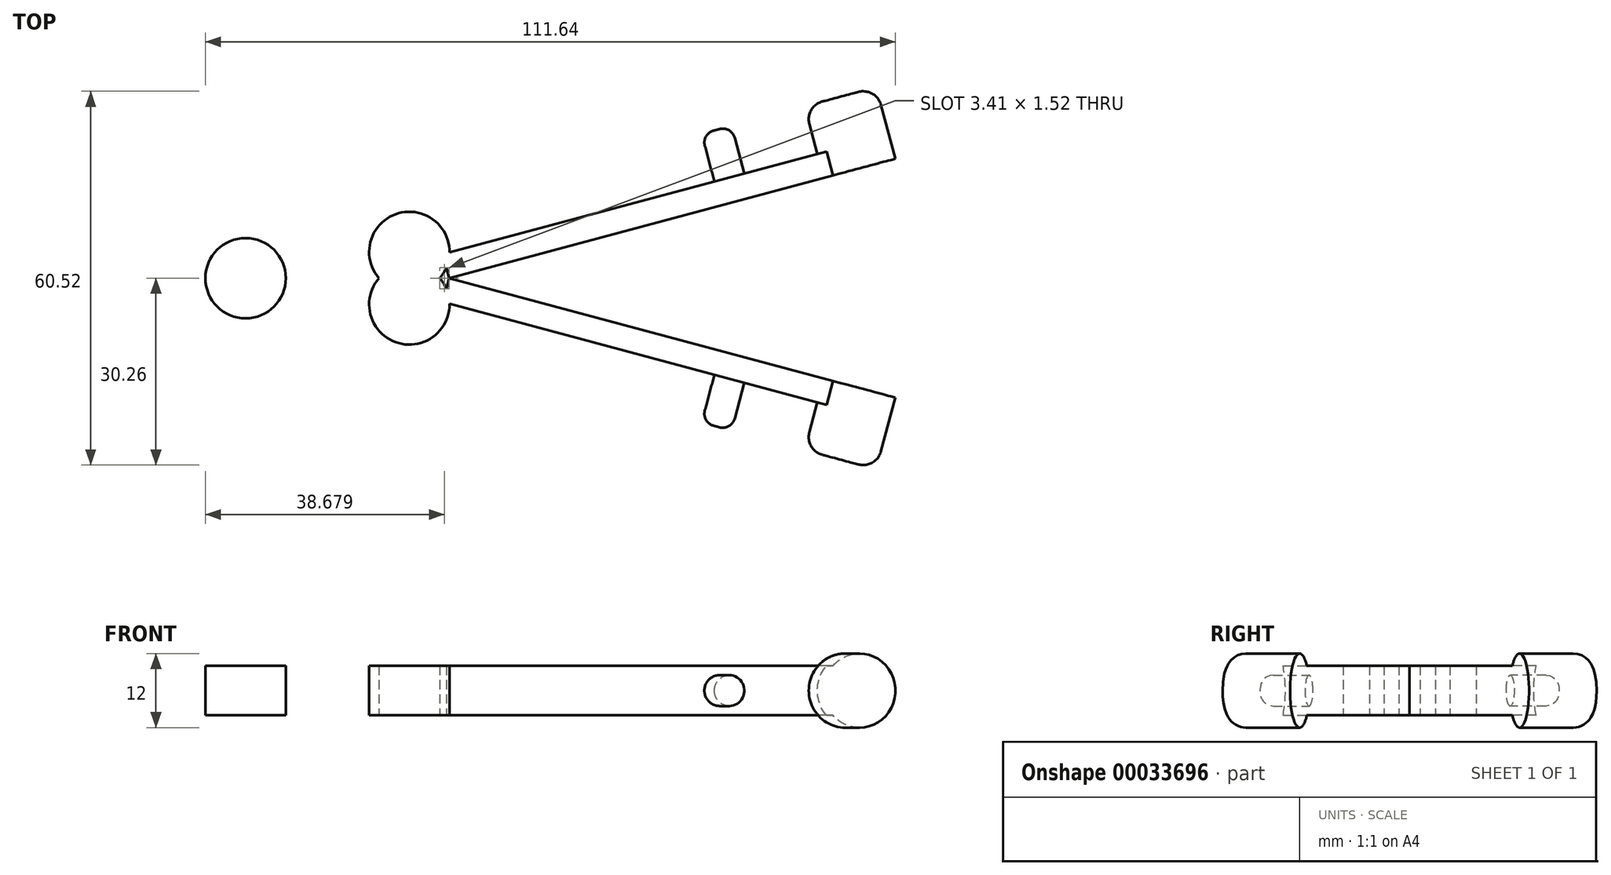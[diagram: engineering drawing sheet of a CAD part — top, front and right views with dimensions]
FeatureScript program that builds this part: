
annotation { "Feature Type Name" : "Feature", "Feature Type Description" : "" }
export const myFeature = defineFeature(function(context is Context, id is Id, definition is map)
    precondition{}
    {
        {
            var Q0;
            Q0=qCreatedBy(makeId("Top.planeOp"),FACE);
            var sketch = newSketch(context, id + "F0", { "sketchPlane" : qUnion([Q0])});
            skCircle(sketch, "E0", {"center": v(-26.5, 0) * mm, "radius": 6.5 * mm});
            skCircle(sketch, "E1", {"center": v(0, 4.25) * mm, "radius": 6.5 * mm});
            skCircle(sketch, "E2.MirrorC", {"center": v(0, -4.25) * mm, "radius": 6.5 * mm});
            skLineSegment(sketch, "E3", {"start": v(-26.3, 6.5) * mm, "end": v(-6.1, 6.5) * mm});
            skLineSegment(sketch, "E4.MirrorCS", {"start": v(-26.3, -6.5) * mm, "end": v(-6.1, -6.5) * mm});
            skLineSegment(sketch, "E5", {"start": v(6.36, 5.61) * mm, "end": v(6.5, -4.15) * mm});
            skLineSegment(sketch, "E6", {"start": v(6.44, 0) * mm, "end": v(47.77, 11.07) * mm});
            skSolve(sketch);
        }
        {
            var Q0;
            {var subQ0=sQuery(id+"F0.wireOp",EDGE,"E0");var subQ2=makeQuery(id+"F0.imprint","INTERSECT",VERTEX,{"derivedFrom":[subQ0,sQuery(id+"F0.wireOp",EDGE,"E3")]});Q0=makeQuery(id+"F0.imprint","IMPRINT",FACE,{"disambiguationData":[TD([[makeQuery(id+"F0.imprint","IMPRINT",EDGE,{"disambiguationData":[TD([[subQ2,-1.0]])],"derivedFrom":subQ0}),1.0]])]});}
            var Q1;
            {var subQ0=sQuery(id+"F0.wireOp",EDGE,"E2.MirrorC");var subQ1=sQuery(id+"F0.wireOp",EDGE,"E1");var subQ3=makeQuery(id+"F0.imprint","INTERSECT",VERTEX,{"disambiguationData":[OD(0.0)],"derivedFrom":[subQ1,subQ0]});Q1=makeQuery(id+"F0.imprint","IMPRINT",FACE,{"disambiguationData":[TD([[makeQuery(id+"F0.imprint","IMPRINT",EDGE,{"disambiguationData":[TD([[subQ3,-1.0]])],"derivedFrom":subQ1}),1.0]])]});}
            var Q2;
            {var subQ0=sQuery(id+"F0.wireOp",EDGE,"E5");var subQ1=sQuery(id+"F0.wireOp",EDGE,"E1");var subQ2=makeQuery(id+"F0.imprint","INTERSECT",VERTEX,{"disambiguationData":[OD(1.0)],"derivedFrom":[subQ1,subQ0]});Q2=makeQuery(id+"F0.imprint","IMPRINT",FACE,{"disambiguationData":[TD([[makeQuery(id+"F0.imprint","IMPRINT",EDGE,{"disambiguationData":[TD([[subQ2,1.0]])],"derivedFrom":subQ1}),-1.0]])]});}
            var Q3;
            {var subQ0=sQuery(id+"F0.wireOp",EDGE,"E3");Q3=makeQuery(id+"F0.imprint","IMPRINT",FACE,{"disambiguationData":[TD([[makeQuery(id+"F0.imprint","IMPRINT",EDGE,{"derivedFrom":subQ0}),-1.0]])]});}
            var Q4;
            {var subQ0=sQuery(id+"F0.wireOp",EDGE,"E2.MirrorC");var subQ3=sQuery(id+"F0.wireOp",EDGE,"E1");var subQ5=makeQuery(id+"F0.imprint","INTERSECT",VERTEX,{"disambiguationData":[OD(0.0)],"derivedFrom":[subQ3,subQ0]});Q4=makeQuery(id+"F0.imprint","IMPRINT",FACE,{"disambiguationData":[TD([[makeQuery(id+"F0.imprint","IMPRINT",EDGE,{"disambiguationData":[TD([[subQ5,-1.0]])],"derivedFrom":subQ3}),-1.0]])]});}
            var Q5;
            {var subQ1=sQuery(id+"F0.wireOp",EDGE,"E1");var subQ7=makeQuery(id+"F0.imprint","INTERSECT",VERTEX,{"derivedFrom":[subQ1,sQuery(id+"F0.wireOp",EDGE,"E3")]});Q5=makeQuery(id+"F0.imprint","IMPRINT",FACE,{"disambiguationData":[TD([[makeQuery(id+"F0.imprint","IMPRINT",EDGE,{"disambiguationData":[TD([[subQ7,1.0]])],"derivedFrom":subQ1}),1.0]])]});}
            var Q6;
            {var subQ0=sQuery(id+"F0.wireOp",EDGE,"E5");var subQ1=sQuery(id+"F0.wireOp",EDGE,"E1");var subQ3=makeQuery(id+"F0.imprint","INTERSECT",VERTEX,{"disambiguationData":[OD(0.0)],"derivedFrom":[subQ1,subQ0]});Q6=makeQuery(id+"F0.imprint","IMPRINT",FACE,{"disambiguationData":[TD([[makeQuery(id+"F0.imprint","IMPRINT",EDGE,{"disambiguationData":[TD([[subQ3,1.0]])],"derivedFrom":subQ1}),1.0]])]});}
            extrude(context, id + "F1", {"entities" : qUnion([Q0, Q1, Q2, Q3, Q4, Q5, Q6]), "depth" : 8 * mm});
        }
        {
            var Q0;
            Q0=sQuery(id+"F0.wireOp",EDGE,"E6");
            cPlane(context, id + "F2", {"entities" : qUnion([Q0]), "cplaneType" : CPlaneType.LINE_ANGLE, "offset" : 150 * mm, "angle" : 0 * degree, "width" : 150 * mm, "height" : 150 * mm});
        }
        {
            var Q0;
            Q0=qCreatedBy(id+"F2.planeOp",FACE);
            var sketch = newSketch(context, id + "F3", { "sketchPlane" : qUnion([Q0])});
            skLineSegment(sketch, "E7.bottom", {"start": v(-74.97, 0) * mm, "end": v(-6.22, 0) * mm});
            skLineSegment(sketch, "E7.top", {"start": v(-74.97, 8) * mm, "end": v(-6.22, 8) * mm});
            skLineSegment(sketch, "E7.left", {"start": v(-74.97, 0) * mm, "end": v(-74.97, 8) * mm});
            skLineSegment(sketch, "E7.right", {"start": v(-6.22, 0) * mm, "end": v(-6.22, 8) * mm});
            skCircle(sketch, "E8", {"center": v(-54.22, 4) * mm, "radius": 2.5 * mm});
            skLineSegment(sketch, "E9", {"start": v(-54.22, 0) * mm, "end": v(-54.22, 8) * mm});
            skLineSegment(sketch, "E10", {"start": v(-54.22, 4) * mm, "end": v(-6.22, 4) * mm});
            skCircle(sketch, "E11", {"center": v(-74.97, 4) * mm, "radius": 6 * mm});
            skLineSegment(sketch, "E12", {"start": v(-70.5, 8) * mm, "end": v(-79.44, 8) * mm});
            skLineSegment(sketch, "E13", {"start": v(-70.5, 0) * mm, "end": v(-79.44, 0) * mm});
            skSolve(sketch);
        }
        {
            var Q0;
            {var subQ5=sQuery(id+"F3.wireOp",EDGE,"E7.left");Q0=makeQuery(id+"F3.imprint","IMPRINT",FACE,{"disambiguationData":[TD([[makeQuery(id+"F3.imprint","IMPRINT",EDGE,{"derivedFrom":subQ5}),1.0]])]});}
            var Q1;
            {var subQ5=sQuery(id+"F3.wireOp",EDGE,"E7.left");Q1=makeQuery(id+"F3.imprint","IMPRINT",FACE,{"disambiguationData":[TD([[makeQuery(id+"F3.imprint","IMPRINT",EDGE,{"derivedFrom":subQ5}),-1.0]])]});}
            var Q2;
            Q2=sQuery(id+"F3.wireOp",EDGE,"8945dfdf-c5bb-4049-810b-f4c16370b47c");
            extrude(context, id + "F4", {"entities" : qUnion([Q0, Q1]), "operationType" : NewBodyOperationType.ADD, "surfaceEntities" : qUnion([Q2]), "depth" : 12 * mm});
        }
        {
            var Q0;
            {var subQ0=sQuery(id+"F3.wireOp",EDGE,"E9");var subQ1=sQuery(id+"F3.wireOp",EDGE,"E8");var subQ2=makeQuery(id+"F3.imprint","INTERSECT",VERTEX,{"disambiguationData":[OD(0.0)],"derivedFrom":[subQ1,subQ0]});Q0=makeQuery(id+"F3.imprint","IMPRINT",FACE,{"disambiguationData":[TD([[makeQuery(id+"F3.imprint","IMPRINT",EDGE,{"disambiguationData":[TD([[subQ2,-1.0]])],"derivedFrom":subQ1}),1.0]])]});}
            var Q1;
            {var subQ1=sQuery(id+"F3.wireOp",EDGE,"E8");var subQ3=sQuery(id+"F3.wireOp",EDGE,"E9");var subQ5=makeQuery(id+"F3.imprint","INTERSECT",VERTEX,{"disambiguationData":[OD(0.0)],"derivedFrom":[subQ1,subQ3]});Q1=makeQuery(id+"F3.imprint","IMPRINT",FACE,{"disambiguationData":[TD([[makeQuery(id+"F3.imprint","IMPRINT",EDGE,{"disambiguationData":[TD([[subQ5,1.0]])],"derivedFrom":subQ1}),1.0]])]});}
            var Q2;
            {var subQ0=sQuery(id+"F3.wireOp",EDGE,"E10");var subQ1=sQuery(id+"F3.wireOp",EDGE,"E8");var subQ2=makeQuery(id+"F3.imprint","INTERSECT",VERTEX,{"derivedFrom":[subQ1,subQ0]});Q2=makeQuery(id+"F3.imprint","IMPRINT",FACE,{"disambiguationData":[TD([[makeQuery(id+"F3.imprint","IMPRINT",EDGE,{"disambiguationData":[TD([[subQ2,1.0]])],"derivedFrom":subQ1}),1.0]])]});}
            var Q3;
            Q3=sQuery(id+"F3.wireOp",EDGE,"E8");
            extrude(context, id + "F5", {"entities" : qUnion([Q0, Q1, Q2]), "operationType" : NewBodyOperationType.ADD, "surfaceEntities" : qUnion([Q3]), "depth" : 12 * mm});
        }
        {
            var Q0;
            {var subQ3=sQuery(id+"F3.wireOp",EDGE,"E7.right");var subQ7=sQuery(id+"F3.wireOp",EDGE,"E7.bottom");var subQ9=makeQuery(id+"F3.imprint","INTERSECT",VERTEX,{"derivedFrom":[subQ7,subQ3]});Q0=makeQuery(id+"F3.imprint","IMPRINT",FACE,{"disambiguationData":[TD([[makeQuery(id+"F3.imprint","IMPRINT",EDGE,{"disambiguationData":[TD([[subQ9,1.0]])],"derivedFrom":subQ7}),1.0]])]});}
            var Q1;
            {var subQ3=sQuery(id+"F3.wireOp",EDGE,"E7.top");var subQ7=sQuery(id+"F3.wireOp",EDGE,"E7.right");var subQ9=makeQuery(id+"F3.imprint","INTERSECT",VERTEX,{"derivedFrom":[subQ3,subQ7]});Q1=makeQuery(id+"F3.imprint","IMPRINT",FACE,{"disambiguationData":[TD([[makeQuery(id+"F3.imprint","IMPRINT",EDGE,{"disambiguationData":[TD([[subQ9,1.0]])],"derivedFrom":subQ3}),-1.0]])]});}
            var Q2;
            {var subQ3=sQuery(id+"F3.wireOp",EDGE,"E7.bottom");var subQ5=sQuery(id+"F3.wireOp",EDGE,"E9");var subQ10=makeQuery(id+"F3.imprint","INTERSECT",VERTEX,{"derivedFrom":[subQ3,subQ5]});Q2=makeQuery(id+"F3.imprint","IMPRINT",FACE,{"disambiguationData":[TD([[makeQuery(id+"F3.imprint","IMPRINT",EDGE,{"disambiguationData":[TD([[subQ10,1.0]])],"derivedFrom":subQ3}),1.0]])]});}
            extrude(context, id + "F6", {"entities" : qUnion([Q0, Q1, Q2]), "depth" : 4 * mm});
        }
        {
            var Q0;
            Q0=makeQuery(id+"F4.opExtrude","CAP_EDGE",EDGE,{"disambiguationData":[OSD([sQuery(id+"F3.wireOp",EDGE,"8945dfdf-c5bb-4049-810b-f4c16370b47c")])],"isStart":false});
            var Q1;
            {var subQ0=sQuery(id+"F3.wireOp",EDGE,"E11");Q1=makeQuery(id+"F4.opExtrude","CAP_EDGE",EDGE,{"disambiguationData":[OSD([subQ0]),TDD([makeQuery(id+"F3.imprint","IMPRINT",EDGE,{"disambiguationData":[TD([[makeQuery(id+"F3.imprint","INTERSECT",VERTEX,{"derivedFrom":[subQ0,sQuery(id+"F3.wireOp",EDGE,"E12")]}),-1.0]])],"derivedFrom":subQ0})])],"isStart":false});}
            fillet(context, id + "F7", {"entities" : qUnion([Q0, Q1]), "radius" : 3 * mm, "tangentPropagation" : true, "allowEdgeOverflow" : false});
        }
        {
            var Q0;
            Q0=makeQuery(id+"F5.opExtrude","CAP_EDGE",EDGE,{"disambiguationData":[OSD([sQuery(id+"F3.wireOp",EDGE,"E8")])],"isStart":false});
            fillet(context, id + "F8", {"entities" : qUnion([Q0]), "radius" : 2 * mm, "tangentPropagation" : true, "allowEdgeOverflow" : false});
        }
        {
            var Q0;
            Q0=makeQuery(id+"F6.opExtrude","SWEPT_BODY",BODY,{"disambiguationData":[OSD([sQuery(id+"F3.wireOp",EDGE,"E7.bottom"),sQuery(id+"F3.wireOp",EDGE,"E7.top"),sQuery(id+"F3.wireOp",EDGE,"E7.right"),sQuery(id+"F3.wireOp",EDGE,"E8"),sQuery(id+"F3.wireOp",EDGE,"E11")])]});
            var Q1;
            Q1=makeQuery(id+"F5.opExtrude","SWEPT_BODY",BODY,{"disambiguationData":[OSD([sQuery(id+"F3.wireOp",EDGE,"E8")])]});
            var Q2;
            Q2=makeQuery(id+"F4.opExtrude","SWEPT_BODY",BODY,{"disambiguationData":[OSD([sQuery(id+"F3.wireOp",EDGE,"E11"),sQuery(id+"F3.wireOp",EDGE,"E12"),sQuery(id+"F3.wireOp",EDGE,"E13")])]});
            var Q3;
            Q3=qCreatedBy(makeId("Front.planeOp"),FACE);
            mirror(context, id + "F9", {"operationType" : NewBodyOperationType.ADD, "entities" : qUnion([Q0, Q1, Q2]), "mirrorPlane" : qUnion([Q3])});
        }
    });
